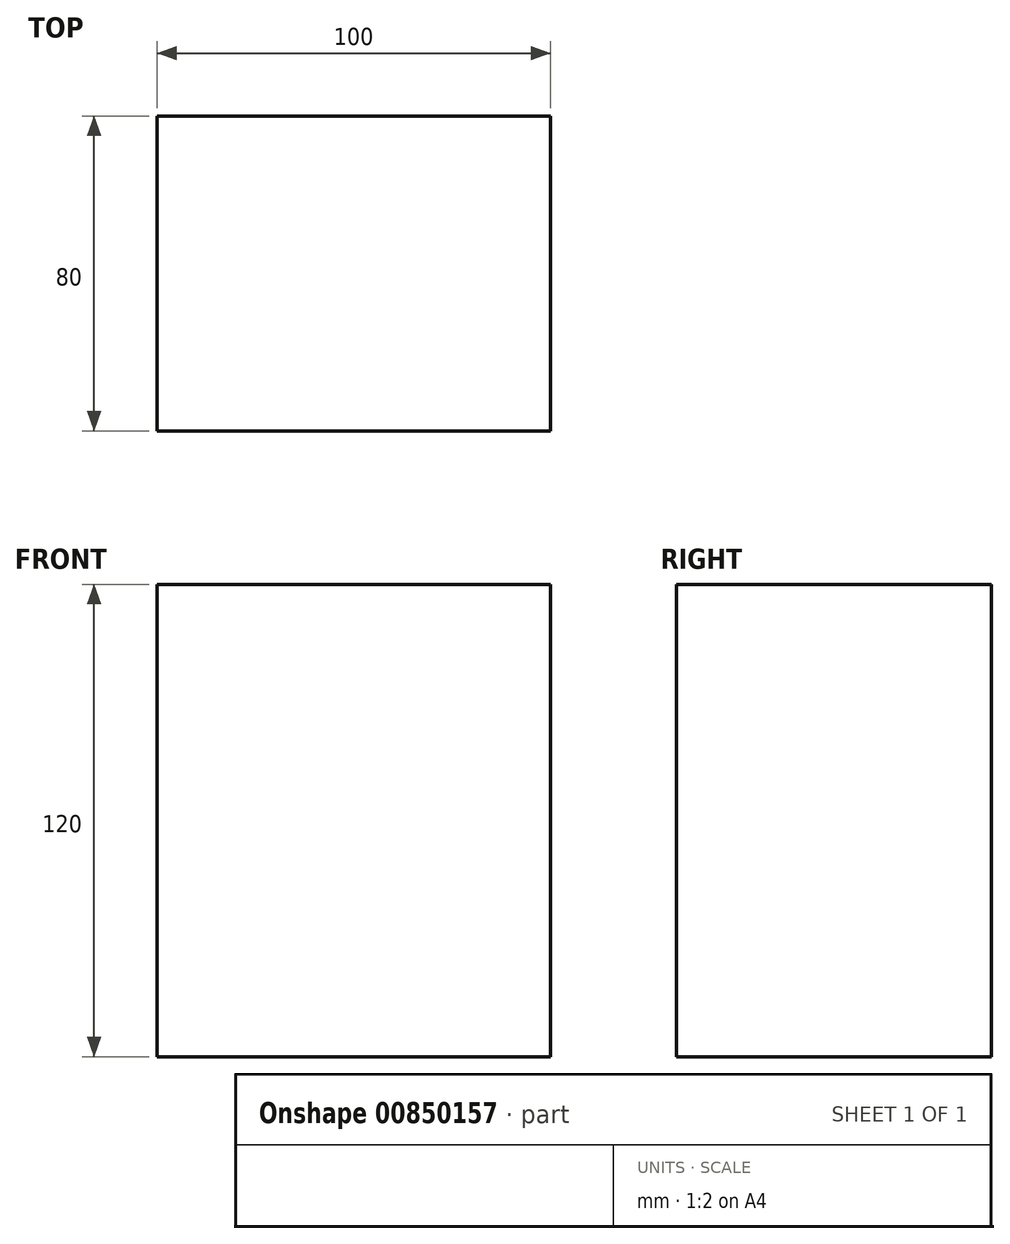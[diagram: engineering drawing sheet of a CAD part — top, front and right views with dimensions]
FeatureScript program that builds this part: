
annotation { "Feature Type Name" : "Feature", "Feature Type Description" : "" }
export const myFeature = defineFeature(function(context is Context, id is Id, definition is map)
    precondition{}
    {
        {
            var Q0;
            Q0=qCreatedBy(makeId("Top.planeOp"),FACE);
            var sketch = newSketch(context, id + "F0", { "sketchPlane" : qUnion([Q0])});
            skLineSegment(sketch, "E0.bottom", {"start": v(-19.41, 25.2) * mm, "end": v(-119.41, 25.2) * mm});
            skLineSegment(sketch, "E0.top", {"start": v(-19.41, 105.2) * mm, "end": v(-119.41, 105.2) * mm});
            skLineSegment(sketch, "E0.left", {"start": v(-19.41, 25.2) * mm, "end": v(-19.41, 105.2) * mm});
            skLineSegment(sketch, "E0.right", {"start": v(-119.41, 25.2) * mm, "end": v(-119.41, 105.2) * mm});
            skPoint(sketch, "E0.middle", {"position": v(-69.41, 65.2) * mm});
            skSolve(sketch);
        }
        {
            var Q0;
            Q0 = qSketchRegion(id + "F0", true);
            extrude(context, id + "F1", {"entities" : qUnion([Q0]), "depth" : 120 * mm, "offsetDistance" : 25 * mm});
        }
    });
